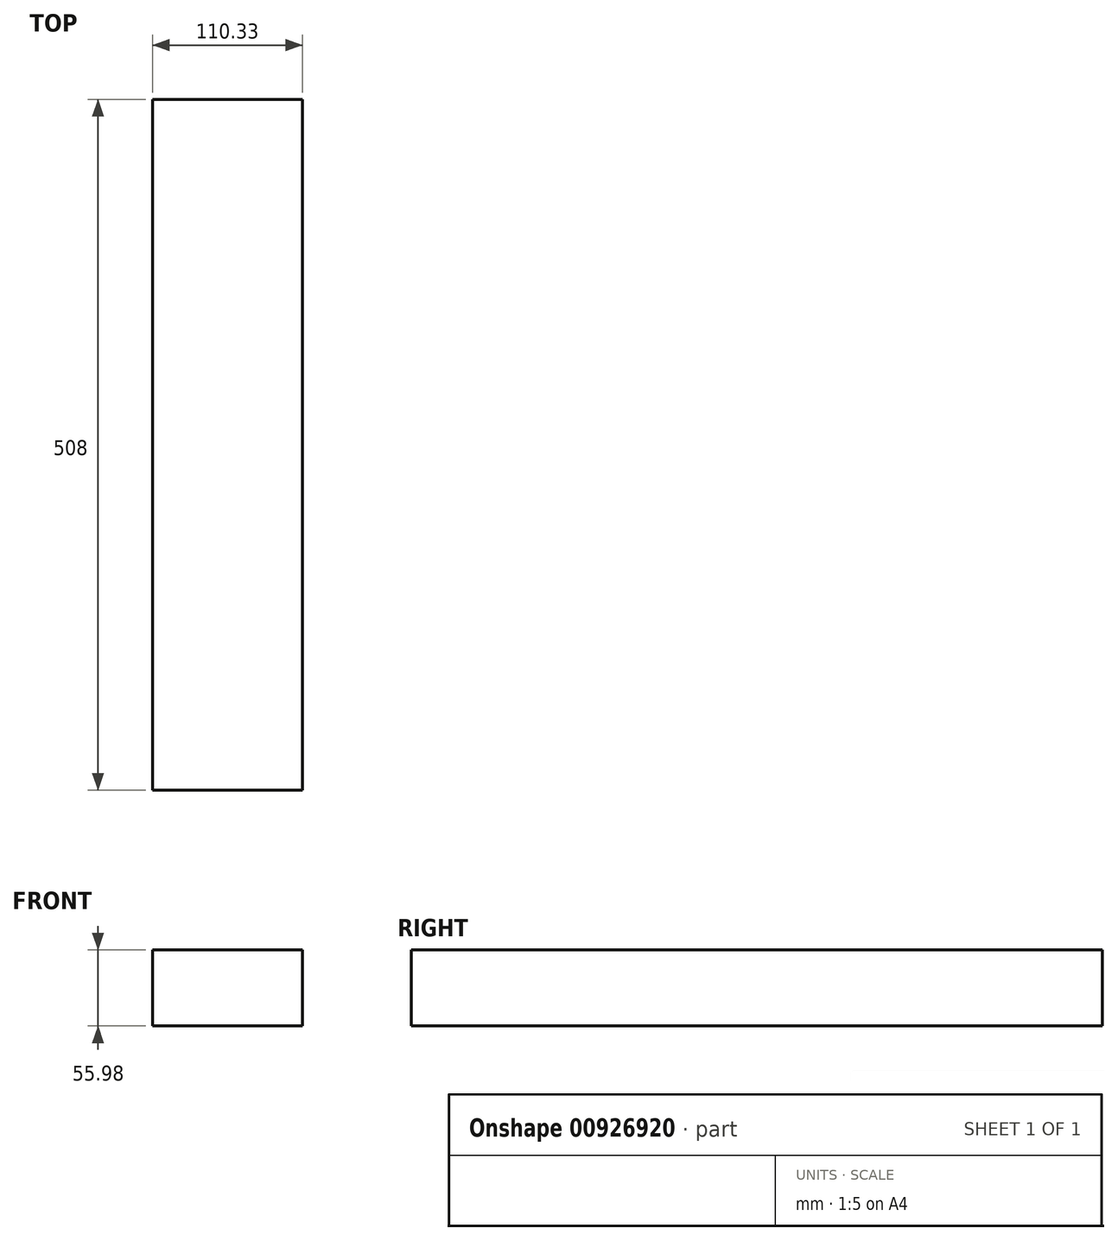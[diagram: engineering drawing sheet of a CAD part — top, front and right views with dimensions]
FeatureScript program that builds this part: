
annotation { "Feature Type Name" : "Feature", "Feature Type Description" : "" }
export const myFeature = defineFeature(function(context is Context, id is Id, definition is map)
    precondition{}
    {
        {
            var Q0;
            Q0=qCreatedBy(makeId("Front.planeOp"),FACE);
            var sketch = newSketch(context, id + "F0", { "sketchPlane" : qUnion([Q0])});
            skLineSegment(sketch, "E0.bottom", {"start": v(-60.3, 44.68) * mm, "end": v(50.03, 44.68) * mm});
            skLineSegment(sketch, "E0.top", {"start": v(-60.3, -11.3) * mm, "end": v(50.03, -11.3) * mm});
            skLineSegment(sketch, "E0.left", {"start": v(-60.3, 44.68) * mm, "end": v(-60.3, -11.3) * mm});
            skLineSegment(sketch, "E0.right", {"start": v(50.03, 44.68) * mm, "end": v(50.03, -11.3) * mm});
            skSolve(sketch);
        }
        {
            var Q0;
            Q0 = qSketchRegion(id + "F0", true);
            extrude(context, id + "F1", {"entities" : qUnion([Q0]), "depth" : 508 * mm, "offsetDistance" : 25.4 * mm});
        }
    });
